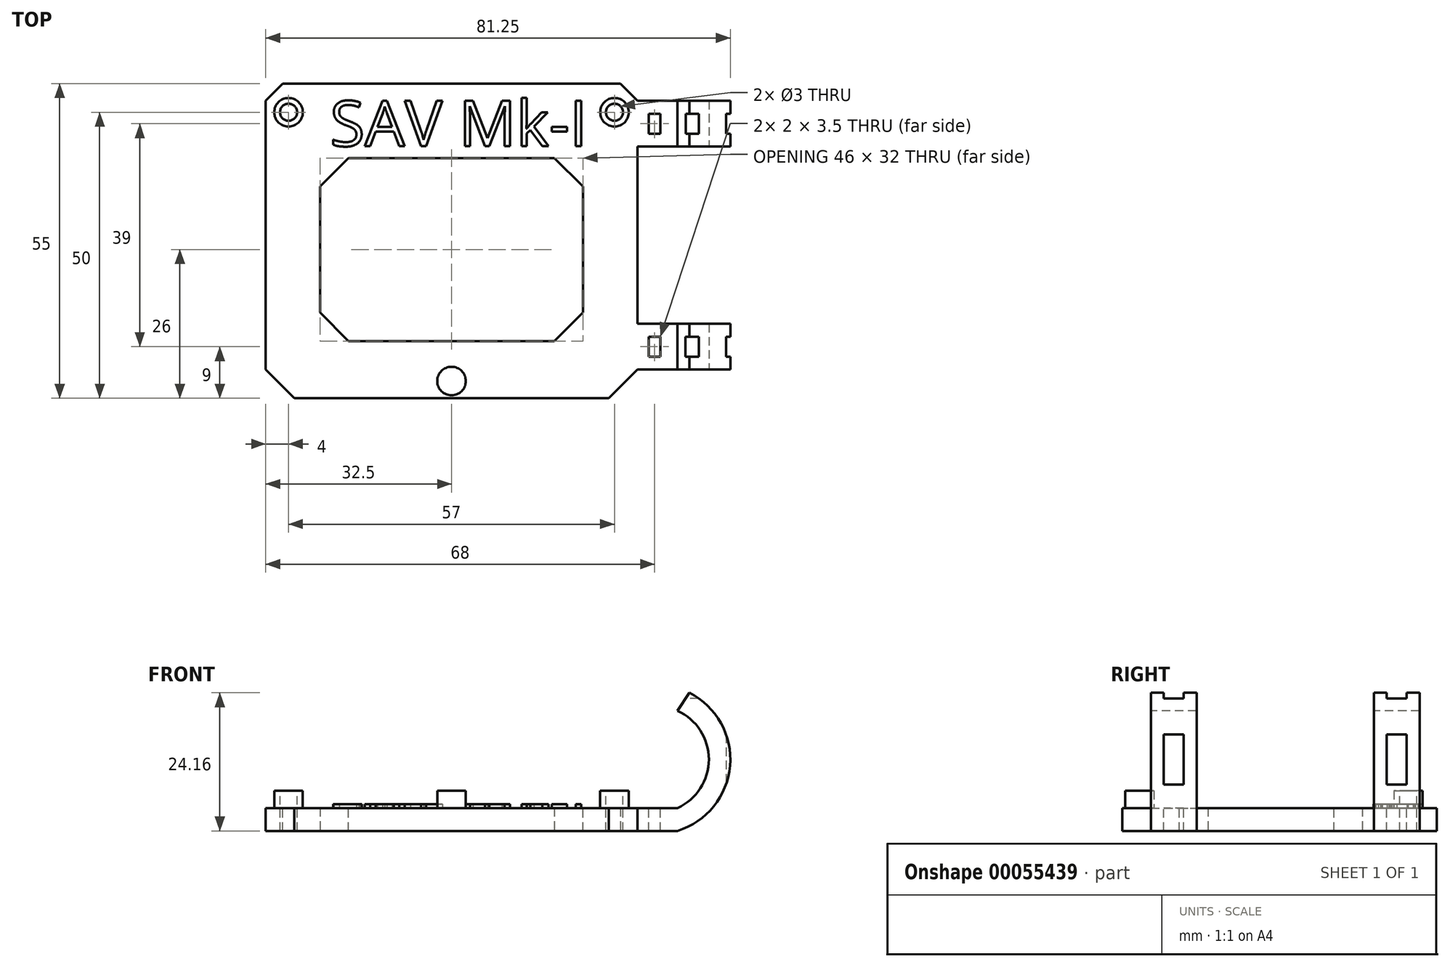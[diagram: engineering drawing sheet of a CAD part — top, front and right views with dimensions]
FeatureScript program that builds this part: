
annotation { "Feature Type Name" : "Feature", "Feature Type Description" : "" }
export const myFeature = defineFeature(function(context is Context, id is Id, definition is map)
    precondition{}
    {
        {
            var Q0;
            Q0=qCreatedBy(makeId("Top.planeOp"),FACE);
            var sketch = newSketch(context, id + "F0", { "sketchPlane" : qUnion([Q0])});
            skLineSegment(sketch, "E0.bottom", {"start": v(0, 0) * mm, "end": v(65, 0) * mm});
            skLineSegment(sketch, "E0.top", {"start": v(0, 55) * mm, "end": v(65, 55) * mm});
            skLineSegment(sketch, "E0.left", {"start": v(0, 0) * mm, "end": v(0, 55) * mm});
            skLineSegment(sketch, "E0.right", {"start": v(65, 0) * mm, "end": v(65, 55) * mm});
            skSolve(sketch);
        }
        {
            var Q0;
            Q0=makeQuery(id+"F0.imprint","IMPRINT",FACE,{"disambiguationData":[TD([[makeQuery(id+"F0.imprint","IMPRINT",EDGE,{"derivedFrom":sQuery(id+"F0.wireOp",EDGE,"E0.bottom")}),1.0]])]});
            extrude(context, id + "F1", {"entities" : qUnion([Q0]), "depth" : 4 * mm});
        }
        {
            var Q0;
            Q0=makeQuery(id+"F1.opExtrude","CAP_FACE",FACE,{"disambiguationData":[OSD([sQuery(id+"F0.wireOp",EDGE,"E0.bottom"),sQuery(id+"F0.wireOp",EDGE,"E0.top"),sQuery(id+"F0.wireOp",EDGE,"E0.left"),sQuery(id+"F0.wireOp",EDGE,"E0.right")])],"isStart":false});
            var sketch = newSketch(context, id + "F2", { "sketchPlane" : qUnion([Q0])});
            skLineSegment(sketch, "E1.bottom", {"start": v(9.5, 10) * mm, "end": v(55.5, 10) * mm});
            skLineSegment(sketch, "E1.top", {"start": v(9.5, 42) * mm, "end": v(55.5, 42) * mm});
            skLineSegment(sketch, "E1.left", {"start": v(9.5, 10) * mm, "end": v(9.5, 42) * mm});
            skLineSegment(sketch, "E1.right", {"start": v(55.5, 10) * mm, "end": v(55.5, 42) * mm});
            skSolve(sketch);
        }
        {
            var Q0;
            Q0=makeQuery(id+"F2.imprint","IMPRINT",FACE,{"disambiguationData":[TD([[makeQuery(id+"F2.imprint","IMPRINT",EDGE,{"derivedFrom":sQuery(id+"F2.wireOp",EDGE,"E1.bottom")}),1.0]])]});
            extrude(context, id + "F3", {"entities" : qUnion([Q0]), "operationType" : NewBodyOperationType.REMOVE, "endBound" : BoundingType.UP_TO_NEXT, "oppositeDirection" : true, "depth" : 25 * mm});
        }
        {
            var Q0;
            Q0=makeQuery(id+"F3.boolean.opBoolean","COPY",EDGE,{"derivedFrom":makeQuery(id+"F3.opExtrude","SWEPT_EDGE",EDGE,{"disambiguationData":[OSD([sQuery(id+"F2.wireOp",EDGE,"E1.top"),sQuery(id+"F2.wireOp",EDGE,"E1.left")])]})});
            var Q1;
            Q1=makeQuery(id+"F3.boolean.opBoolean","COPY",EDGE,{"derivedFrom":makeQuery(id+"F3.opExtrude","SWEPT_EDGE",EDGE,{"disambiguationData":[OSD([sQuery(id+"F2.wireOp",EDGE,"E1.top"),sQuery(id+"F2.wireOp",EDGE,"E1.right")])]})});
            var Q2;
            Q2=makeQuery(id+"F3.boolean.opBoolean","COPY",EDGE,{"derivedFrom":makeQuery(id+"F3.opExtrude","SWEPT_EDGE",EDGE,{"disambiguationData":[OSD([sQuery(id+"F2.wireOp",EDGE,"E1.bottom"),sQuery(id+"F2.wireOp",EDGE,"E1.left")])]})});
            var Q3;
            Q3=makeQuery(id+"F3.boolean.opBoolean","COPY",EDGE,{"derivedFrom":makeQuery(id+"F3.opExtrude","SWEPT_EDGE",EDGE,{"disambiguationData":[OSD([sQuery(id+"F2.wireOp",EDGE,"E1.bottom"),sQuery(id+"F2.wireOp",EDGE,"E1.right")])]})});
            chamfer(context, id + "F4", {"entities" : qUnion([Q0, Q1, Q2, Q3]), "width" : 5 * mm, "tangentPropagation" : true});
        }
        {
            var Q0;
            Q0=makeQuery(id+"F1.opExtrude","CAP_FACE",FACE,{"disambiguationData":[OSD([sQuery(id+"F0.wireOp",EDGE,"E0.bottom"),sQuery(id+"F0.wireOp",EDGE,"E0.top"),sQuery(id+"F0.wireOp",EDGE,"E0.left"),sQuery(id+"F0.wireOp",EDGE,"E0.right")])],"isStart":false});
            var sketch = newSketch(context, id + "F5", { "sketchPlane" : qUnion([Q0])});
            skCircle(sketch, "E2", {"center": v(4, 50) * mm, "radius": 2.5 * mm});
            skCircle(sketch, "E3", {"center": v(61, 50) * mm, "radius": 2.5 * mm});
            skCircle(sketch, "E4", {"center": v(32.5, 3) * mm, "radius": 2.5 * mm});
            skSolve(sketch);
        }
        {
            var Q0;
            Q0=makeQuery(id+"F5.imprint","IMPRINT",FACE,{"disambiguationData":[TD([[makeQuery(id+"F5.imprint","IMPRINT",EDGE,{"derivedFrom":sQuery(id+"F5.wireOp",EDGE,"E4")}),1.0]])]});
            var Q1;
            Q1=makeQuery(id+"F5.imprint","IMPRINT",FACE,{"disambiguationData":[TD([[makeQuery(id+"F5.imprint","IMPRINT",EDGE,{"derivedFrom":sQuery(id+"F5.wireOp",EDGE,"E2")}),1.0]])]});
            var Q2;
            Q2=makeQuery(id+"F5.imprint","IMPRINT",FACE,{"disambiguationData":[TD([[makeQuery(id+"F5.imprint","IMPRINT",EDGE,{"derivedFrom":sQuery(id+"F5.wireOp",EDGE,"E3")}),1.0]])]});
            extrude(context, id + "F6", {"entities" : qUnion([Q0, Q1, Q2]), "operationType" : NewBodyOperationType.ADD, "depth" : 3 * mm});
        }
        {
            var Q0;
            Q0=makeQuery(id+"F6.opExtrude","CAP_FACE",FACE,{"disambiguationData":[OSD([sQuery(id+"F5.wireOp",EDGE,"E2")])],"isStart":false});
            var sketch = newSketch(context, id + "F7", { "sketchPlane" : qUnion([Q0])});
            skPoint(sketch, "E5", {"position": v(4, 50) * mm});
            skSolve(sketch);
        }
        {
            var Q0;
            Q0=makeQuery(id+"F6.opExtrude","CAP_FACE",FACE,{"disambiguationData":[OSD([sQuery(id+"F5.wireOp",EDGE,"E3")])],"isStart":false});
            var sketch = newSketch(context, id + "F8", { "sketchPlane" : qUnion([Q0])});
            skPoint(sketch, "E6", {"position": v(61, 50) * mm});
            skSolve(sketch);
        }
        {
            var Q0;
            Q0=sQuery(id+"F7.wireOp",VERTEX,"E5");
            var Q1;
            Q1=sQuery(id+"F8.wireOp",VERTEX,"E6");
            var Q2;
            Q2=makeQuery(id+"F1.opExtrude","SWEPT_BODY",BODY,{"disambiguationData":[OSD([sQuery(id+"F0.wireOp",EDGE,"E0.bottom"),sQuery(id+"F0.wireOp",EDGE,"E0.top"),sQuery(id+"F0.wireOp",EDGE,"E0.left"),sQuery(id+"F0.wireOp",EDGE,"E0.right")])]});
            hole(context, id + "F9", {"style" : HoleStyle.SIMPLE, "holeDiameter" : 3 * mm, "endStyle" : HoleEndStyle.THROUGH, "locations" : qUnion([Q0, Q1]), "scope" : qUnion([Q2])});
        }
        {
            var Q0;
            Q0=makeQuery(id+"F1.opExtrude","CAP_FACE",FACE,{"disambiguationData":[OSD([sQuery(id+"F0.wireOp",EDGE,"E0.bottom"),sQuery(id+"F0.wireOp",EDGE,"E0.top"),sQuery(id+"F0.wireOp",EDGE,"E0.left"),sQuery(id+"F0.wireOp",EDGE,"E0.right")])],"isStart":false});
            var sketch = newSketch(context, id + "F10", { "sketchPlane" : qUnion([Q0])});
            skLineSegment(sketch, "E7", {"start": v(65, 44) * mm, "end": v(72, 44) * mm});
            skLineSegment(sketch, "E8", {"start": v(72, 44) * mm, "end": v(72, 52) * mm});
            skLineSegment(sketch, "E9", {"start": v(72, 52) * mm, "end": v(65, 52) * mm});
            skLineSegment(sketch, "E10", {"start": v(65, 5) * mm, "end": v(72, 5) * mm});
            skLineSegment(sketch, "E11", {"start": v(72, 5) * mm, "end": v(72, 13) * mm});
            skLineSegment(sketch, "E12", {"start": v(72, 13) * mm, "end": v(65, 13) * mm});
            skSolve(sketch);
        }
        {
            var Q0;
            {var subQ0=sQuery(id+"F10.wireOp",EDGE,"E7");Q0=makeQuery(id+"F10.imprint","IMPRINT",FACE,{"disambiguationData":[TD([[makeQuery(id+"F10.imprint","IMPRINT",EDGE,{"derivedFrom":subQ0}),1.0]])]});}
            var Q1;
            {var subQ0=sQuery(id+"F10.wireOp",EDGE,"E10");Q1=makeQuery(id+"F10.imprint","IMPRINT",FACE,{"disambiguationData":[TD([[makeQuery(id+"F10.imprint","IMPRINT",EDGE,{"derivedFrom":subQ0}),1.0]])]});}
            extrude(context, id + "F11", {"entities" : qUnion([Q0, Q1]), "operationType" : NewBodyOperationType.ADD, "oppositeDirection" : true, "depth" : 4 * mm});
        }
        {
            var Q0;
            Q0=makeQuery(id+"F1.opExtrude","SWEPT_EDGE",EDGE,{"disambiguationData":[OSD([sQuery(id+"F0.wireOp",EDGE,"E0.bottom"),sQuery(id+"F0.wireOp",EDGE,"E0.right")])]});
            chamfer(context, id + "F12", {"entities" : qUnion([Q0]), "width" : 5 * mm, "tangentPropagation" : true});
        }
        {
            var Q0;
            Q0=makeQuery(id+"F1.opExtrude","SWEPT_EDGE",EDGE,{"disambiguationData":[OSD([sQuery(id+"F0.wireOp",EDGE,"E0.top"),sQuery(id+"F0.wireOp",EDGE,"E0.right")])]});
            chamfer(context, id + "F13", {"entities" : qUnion([Q0]), "width" : 3 * mm, "tangentPropagation" : true});
        }
        {
            var Q0;
            Q0=makeQuery(id+"F1.opExtrude","SWEPT_EDGE",EDGE,{"disambiguationData":[OSD([sQuery(id+"F0.wireOp",EDGE,"E0.bottom"),sQuery(id+"F0.wireOp",EDGE,"E0.left")])]});
            chamfer(context, id + "F14", {"entities" : qUnion([Q0]), "width" : 5 * mm, "tangentPropagation" : true});
        }
        {
            var Q0;
            Q0=makeQuery(id+"F1.opExtrude","SWEPT_EDGE",EDGE,{"disambiguationData":[OSD([sQuery(id+"F0.wireOp",EDGE,"E0.top"),sQuery(id+"F0.wireOp",EDGE,"E0.left")])]});
            chamfer(context, id + "F15", {"entities" : qUnion([Q0]), "width" : 3 * mm, "tangentPropagation" : true});
        }
        {
            var Q0;
            {var subQ0=sQuery(id+"F0.wireOp",EDGE,"E0.right");Q0=makeQuery(id+"F11.boolean.opBoolean","MERGE",FACE,{"derivedFrom":[makeQuery(id+"F1.opExtrude","CAP_FACE",FACE,{"disambiguationData":[OSD([sQuery(id+"F0.wireOp",EDGE,"E0.bottom"),sQuery(id+"F0.wireOp",EDGE,"E0.top"),sQuery(id+"F0.wireOp",EDGE,"E0.left"),subQ0])],"isStart":false}),makeQuery(id+"F11.opExtrude","CAP_FACE",FACE,{"disambiguationData":[OSD([subQ0,sQuery(id+"F10.wireOp",EDGE,"E7"),sQuery(id+"F10.wireOp",EDGE,"E8"),sQuery(id+"F10.wireOp",EDGE,"E9")])],"isStart":true}),makeQuery(id+"F11.opExtrude","CAP_FACE",FACE,{"disambiguationData":[OSD([subQ0,sQuery(id+"F10.wireOp",EDGE,"E10"),sQuery(id+"F10.wireOp",EDGE,"E11"),sQuery(id+"F10.wireOp",EDGE,"E12")])],"isStart":true})]});}
            var sketch = newSketch(context, id + "F16", { "sketchPlane" : qUnion([Q0])});
            skText(sketch, "E13", { "text": "SAV Mk-I", "fontName": "OpenSans-Regular.ttf"});
            const initialGuessF16  = {"E13": [0.01125, 0.04408, 1, 0, 0.00797]};
            skSetInitialGuess(sketch, initialGuessF16);
            skSolve(sketch);
        }
        {
            var Q0;
            Q0 = qSketchRegion(id + "F16", true);
            extrude(context, id + "F17", {"entities" : qUnion([Q0]), "operationType" : NewBodyOperationType.ADD, "depth" : 0.7 * mm});
        }
        {
            var Q0;
            Q0=makeQuery(id+"F11.opExtrude","SWEPT_FACE",FACE,{"disambiguationData":[OSD([sQuery(id+"F10.wireOp",EDGE,"E10")])]});
            var sketch = newSketch(context, id + "F18", { "sketchPlane" : qUnion([Q0])});
            skArc(sketch, "E14", {"start": v(72, 4) * mm, "mid": v(77.5, 12.5) * mm, "end": v(72, 21) * mm});
            skArc(sketch, "E15", {"start": v(72, 0) * mm, "mid": v(81.2, 11.38) * mm, "end": v(74.09, 24.16) * mm});
            skLineSegment(sketch, "E16", {"start": v(72, 21) * mm, "end": v(74.09, 24.16) * mm});
            skSolve(sketch);
        }
        {
            var Q0;
            Q0=makeQuery(id+"F18.imprint","IMPRINT",FACE,{"disambiguationData":[TD([[makeQuery(id+"F18.imprint","IMPRINT",EDGE,{"derivedFrom":sQuery(id+"F18.wireOp",EDGE,"E14")}),-1.0]])]});
            extrude(context, id + "F19", {"entities" : qUnion([Q0]), "operationType" : NewBodyOperationType.ADD, "oppositeDirection" : true, "depth" : 8 * mm});
        }
        {
            var Q0;
            Q0=makeQuery(id+"F11.opExtrude","SWEPT_FACE",FACE,{"disambiguationData":[OSD([sQuery(id+"F10.wireOp",EDGE,"E7")])]});
            var sketch = newSketch(context, id + "F20", { "sketchPlane" : qUnion([Q0])});
            skArc(sketch, "E17", {"start": v(72, 4) * mm, "mid": v(77.5, 12.5) * mm, "end": v(72, 21) * mm});
            skArc(sketch, "E18", {"start": v(72, 0) * mm, "mid": v(81.2, 11.35) * mm, "end": v(74.12, 24.14) * mm});
            skLineSegment(sketch, "E19", {"start": v(72, 21) * mm, "end": v(74.12, 24.14) * mm});
            skSolve(sketch);
        }
        {
            var Q0;
            Q0=makeQuery(id+"F20.imprint","IMPRINT",FACE,{"disambiguationData":[TD([[makeQuery(id+"F20.imprint","IMPRINT",EDGE,{"derivedFrom":sQuery(id+"F20.wireOp",EDGE,"E17")}),-1.0]])]});
            extrude(context, id + "F21", {"entities" : qUnion([Q0]), "operationType" : NewBodyOperationType.ADD, "oppositeDirection" : true, "depth" : 8 * mm});
        }
        {
            var Q0;
            Q0=qCreatedBy(makeId("Top.planeOp"),FACE);
            var sketch = newSketch(context, id + "F22", { "sketchPlane" : qUnion([Q0])});
            skLineSegment(sketch, "E20.bottom", {"start": v(80.5, 49.75) * mm, "end": v(86.15, 49.75) * mm});
            skLineSegment(sketch, "E20.top", {"start": v(80.5, 46.25) * mm, "end": v(86.15, 46.25) * mm});
            skLineSegment(sketch, "E20.left", {"start": v(80.5, 49.75) * mm, "end": v(80.5, 46.25) * mm});
            skLineSegment(sketch, "E20.right", {"start": v(86.15, 49.75) * mm, "end": v(86.15, 46.25) * mm});
            skLineSegment(sketch, "E21.bottom", {"start": v(80.5, 10.75) * mm, "end": v(87.57, 10.75) * mm});
            skLineSegment(sketch, "E21.top", {"start": v(80.5, 7.25) * mm, "end": v(87.57, 7.25) * mm});
            skLineSegment(sketch, "E21.left", {"start": v(80.5, 10.75) * mm, "end": v(80.5, 7.25) * mm});
            skLineSegment(sketch, "E21.right", {"start": v(87.57, 10.75) * mm, "end": v(87.57, 7.25) * mm});
            skSolve(sketch);
        }
        {
            var Q0;
            Q0=makeQuery(id+"F22.imprint","IMPRINT",FACE,{"disambiguationData":[TD([[makeQuery(id+"F22.imprint","IMPRINT",EDGE,{"derivedFrom":sQuery(id+"F22.wireOp",EDGE,"E21.bottom")}),-1.0]])]});
            var Q1;
            Q1=makeQuery(id+"F22.imprint","IMPRINT",FACE,{"disambiguationData":[TD([[makeQuery(id+"F22.imprint","IMPRINT",EDGE,{"derivedFrom":sQuery(id+"F22.wireOp",EDGE,"E20.bottom")}),-1.0]])]});
            extrude(context, id + "F23", {"entities" : qUnion([Q0, Q1]), "operationType" : NewBodyOperationType.REMOVE, "endBound" : BoundingType.THROUGH_ALL, "depth" : 25 * mm});
        }
        {
            var Q0;
            {var subQ2=sQuery(id+"F10.wireOp",EDGE,"E10");var subQ5=sQuery(id+"F0.wireOp",EDGE,"E0.bottom");var subQ6=sQuery(id+"F10.wireOp",EDGE,"E11");var subQ7=sQuery(id+"F10.wireOp",EDGE,"E8");var subQ8=sQuery(id+"F0.wireOp",EDGE,"E0.right");var subQ9=sQuery(id+"F10.wireOp",EDGE,"E12");var subQ10=sQuery(id+"F10.wireOp",EDGE,"E9");var subQ11=sQuery(id+"F0.wireOp",EDGE,"E0.top");var subQ12=sQuery(id+"F0.wireOp",EDGE,"E0.left");var subQ13=sQuery(id+"F10.wireOp",EDGE,"E7");Q0=makeQuery(id+"F17.boolean.opBoolean","SPLIT",FACE,{"disambiguationData":[TD([makeQuery(id+"F1.opExtrude","SWEPT_FACE",FACE,{"disambiguationData":[OSD([subQ5])]})])],"derivedFrom":makeQuery(id+"F11.boolean.opBoolean","MERGE",FACE,{"derivedFrom":[makeQuery(id+"F1.opExtrude","CAP_FACE",FACE,{"disambiguationData":[OSD([subQ5,subQ11,subQ12,subQ8])],"isStart":false}),makeQuery(id+"F11.opExtrude","CAP_FACE",FACE,{"disambiguationData":[OSD([subQ8,subQ13,subQ7,subQ10])],"isStart":true}),makeQuery(id+"F11.opExtrude","CAP_FACE",FACE,{"disambiguationData":[OSD([subQ8,subQ2,subQ6,subQ9])],"isStart":true})]})});}
            var sketch = newSketch(context, id + "F24", { "sketchPlane" : qUnion([Q0])});
            skLineSegment(sketch, "E22.bottom", {"start": v(67, 49.75) * mm, "end": v(69, 49.75) * mm});
            skLineSegment(sketch, "E22.top", {"start": v(67, 46.25) * mm, "end": v(69, 46.25) * mm});
            skLineSegment(sketch, "E22.left", {"start": v(67, 49.75) * mm, "end": v(67, 46.25) * mm});
            skLineSegment(sketch, "E22.right", {"start": v(69, 49.75) * mm, "end": v(69, 46.25) * mm});
            skLineSegment(sketch, "E23.bottom", {"start": v(67, 10.75) * mm, "end": v(69, 10.75) * mm});
            skLineSegment(sketch, "E23.top", {"start": v(67, 7.25) * mm, "end": v(69, 7.25) * mm});
            skLineSegment(sketch, "E23.left", {"start": v(67, 10.75) * mm, "end": v(67, 7.25) * mm});
            skLineSegment(sketch, "E23.right", {"start": v(69, 10.75) * mm, "end": v(69, 7.25) * mm});
            skSolve(sketch);
        }
        {
            var Q0;
            Q0=makeQuery(id+"F24.imprint","IMPRINT",FACE,{"disambiguationData":[TD([[makeQuery(id+"F24.imprint","IMPRINT",EDGE,{"derivedFrom":sQuery(id+"F24.wireOp",EDGE,"E23.bottom")}),-1.0]])]});
            var Q1;
            Q1=makeQuery(id+"F24.imprint","IMPRINT",FACE,{"disambiguationData":[TD([[makeQuery(id+"F24.imprint","IMPRINT",EDGE,{"derivedFrom":sQuery(id+"F24.wireOp",EDGE,"E22.bottom")}),-1.0]])]});
            extrude(context, id + "F25", {"entities" : qUnion([Q0, Q1]), "operationType" : NewBodyOperationType.REMOVE, "endBound" : BoundingType.THROUGH_ALL, "oppositeDirection" : true, "depth" : 25 * mm});
        }
        {
            var Q0;
            Q0=qCreatedBy(makeId("Right.planeOp"),FACE);
            var sketch = newSketch(context, id + "F26", { "sketchPlane" : qUnion([Q0])});
            skLineSegment(sketch, "E24.bottom", {"start": v(7.25, 29.03) * mm, "end": v(10.75, 29.03) * mm});
            skLineSegment(sketch, "E24.top", {"start": v(7.25, 23.16) * mm, "end": v(10.75, 23.16) * mm});
            skLineSegment(sketch, "E24.left", {"start": v(7.25, 29.03) * mm, "end": v(7.25, 23.16) * mm});
            skLineSegment(sketch, "E24.right", {"start": v(10.75, 29.03) * mm, "end": v(10.75, 23.16) * mm});
            skLineSegment(sketch, "E25.bottom", {"start": v(46.25, 23.16) * mm, "end": v(49.75, 23.16) * mm});
            skLineSegment(sketch, "E25.top", {"start": v(46.25, 28.77) * mm, "end": v(49.75, 28.77) * mm});
            skLineSegment(sketch, "E25.left", {"start": v(46.25, 23.16) * mm, "end": v(46.25, 28.77) * mm});
            skLineSegment(sketch, "E25.right", {"start": v(49.75, 23.16) * mm, "end": v(49.75, 28.77) * mm});
            skSolve(sketch);
        }
        {
            var Q0;
            Q0=makeQuery(id+"F26.imprint","IMPRINT",FACE,{"disambiguationData":[TD([[makeQuery(id+"F26.imprint","IMPRINT",EDGE,{"derivedFrom":sQuery(id+"F26.wireOp",EDGE,"E24.bottom")}),-1.0]])]});
            var Q1;
            Q1=makeQuery(id+"F26.imprint","IMPRINT",FACE,{"disambiguationData":[TD([[makeQuery(id+"F26.imprint","IMPRINT",EDGE,{"derivedFrom":sQuery(id+"F26.wireOp",EDGE,"E25.bottom")}),1.0]])]});
            extrude(context, id + "F27", {"entities" : qUnion([Q0, Q1]), "operationType" : NewBodyOperationType.REMOVE, "endBound" : BoundingType.THROUGH_ALL, "depth" : 25 * mm});
        }
    });
